# Revit family: 111110001403001
name_source: partatom
category: Generic Models
revit_build: Autodesk Revit 2018 (Build: 20190510_1515(x64)
units: mm (PartAtom-declared; Revit-internal decimal feet)

## family parameters
Can host rebar = No
Cut with Voids When Loaded = No
Host = Face
Part Type = Normal
Room Calculation Point = No
Round Connector Dimension = Use Diameter
Shared = No

## types (1)
- CELOSIA PLANA PP 20X20CM BLANCO
    Aplicacion = Se utiliza como sistema de ventilación en puertas, muro y tinas.
    Color = Blanco
    Default Elevation = 1 m
    Description = Celosía plana 20x20
    Dimension = 20 m
    Empresa = CNP SPA.
    Espesor = 1 m
    Largo = 20 m
    Material = PP Blanco
    Model = CELOSIA PLANA
    Nombre SKU = CELOSIA PLANA PP 20X20CM BLANCO
    Num SKUs = 111110001403001
    URL = https://www.empresascnp.cl
    Unidad = Cajas de 50 Unidades
    Url Ficha tecnica = https://empresascnp.cl
    Uso = Se utiliza como sistema de ventilación en Puertas, Shaft, Muro y Tina

## geometry (parser evidence)
native form markers: Sweep x9
no freeform markers — native parametric forms only
